# Revit family: Green Dot Sign® ADA Pictogram
name_source: partatom
category: Generic Models
units: mm (PartAtom-declared; Revit-internal decimal feet)

## family parameters
Always vertical = Yes
Can host rebar = No
Cut with Voids When Loaded = No
Host = Wall
Part Type = Normal
Room Calculation Point = No
Round Connector Dimension = Use Diameter
Shared = No

## types (48) — shared parameters
Height = 0' - 9 1/4"
Text Height = 0' - 0 5/8"
Text Line 3 = SAMPLE TEXT
Text Spacing = 0' - 0 3/8"
URL = https://www.greendotsign.com

## per-type parameters (varying)
| type | All Gender | All Gender Left | All Gender Right | Base Finish | Braille Finish | Chamfered Edge | Eased Edge | Men Restroom | Men Restroom Left | Men Restroom Right | Pictogram Finish | Text Block Height | Text Finish | Text Line 1 | Text Line 2 | Text Number of Lines | Thickness | Unisex Restroom | Unisex Restroom Left | Unisex Restroom Right | Width | Women Restroom | Women Restroom Left | Women Restroom Right |
| Aluminum Unisex Restroom Right 9.25 x 7.25 | No | No | No | Green Dot Sign® Red | Green Dot Sign® Red | No | Yes | No | No | No | Green Dot Sign® Aluminum | 0' - 2" | Green Dot Sign® Aluminum | RESTROOM | SAMPLE TEXT | 1 | 0' - 0 3/16" | No | No | Yes | 0' - 7 1/4" | No | No | No |
| Aluminum Unisex Restroom Left 9.25 x 7.25 | No | No | No | Green Dot Sign® Black | Green Dot Sign® Black | No | Yes | No | No | No | Green Dot Sign® Aluminum | 0' - 2" | Green Dot Sign® Aluminum | RESTROOM | SAMPLE TEXT | 1 | 0' - 0 3/16" | No | Yes | No | 0' - 7 1/4" | No | No | No |
| Aluminum All Gender Restroom Right 9.25 x 7.25 | No | No | No | Green Dot Sign® Red | Green Dot Sign® Red | No | Yes | No | No | Yes | Green Dot Sign® Aluminum | 0' - 2 3/4" | Green Dot Sign® Aluminum | ALL GENDER | RESTROOM | 2 | 0' - 0 3/16" | No | No | No | 0' - 7 1/4" | No | No | No |
| Aluminum All Gender Restroom Left 9.25 x 7.25 | No | Yes | No | Green Dot Sign® Black | Green Dot Sign® Black | No | Yes | No | No | No | Green Dot Sign® Aluminum | 0' - 2 3/4" | Green Dot Sign® Aluminum | ALL GENDER | RESTROOM | 2 | 0' - 0 3/16" | No | No | No | 0' - 7 1/4" | No | No | No |
| Aluminum Unisex Restroom 9.25 x 9.25 | No | No | No | Green Dot Sign® Black | Green Dot Sign® Black | No | Yes | No | No | No | Green Dot Sign® Aluminum | 0' - 2" | Green Dot Sign® Aluminum | RESTROOM | SAMPLE TEXT | 1 | 0' - 0 3/16" | Yes | No | No | 0' - 9 1/4" | No | No | No |
| Aluminum All Gender Restroom 9.25 x 7.25 | Yes | No | No | Green Dot Sign® Black | Green Dot Sign® Black | No | Yes | No | No | No | Green Dot Sign® Aluminum | 0' - 2 3/4" | Green Dot Sign® Aluminum | ALL GENDER | RESTROOM | 2 | 0' - 0 3/16" | No | No | No | 0' - 7 1/4" | No | No | No |
| Aluminum Women Restroom Right 9.25 x 7.25 | No | No | No | Green Dot Sign® Red | Green Dot Sign® Red | No | Yes | No | No | No | Green Dot Sign® Bronze | 0' - 2" | Green Dot Sign® Bronze | WOMEN | SAMPLE TEXT | 1 | 0' - 0 3/16" | No | No | No | 0' - 7 1/4" | No | No | Yes |
| Aluminum Women Restroom Left 9.25 x 7.25 | No | No | No | Green Dot Sign® Black | Green Dot Sign® Black | No | Yes | No | No | No | Green Dot Sign® Bronze | 0' - 2" | Green Dot Sign® Bronze | WOMEN | SAMPLE TEXT | 1 | 0' - 0 3/16" | No | No | No | 0' - 7 1/4" | No | Yes | No |
| Aluminum Men Restroom Right 9.25 x 7.25 | No | No | No | Green Dot Sign® Red | Green Dot Sign® Red | No | Yes | No | No | Yes | Green Dot Sign® Aluminum | 0' - 2" | Green Dot Sign® Aluminum | MEN | SAMPLE TEXT | 1 | 0' - 0 3/16" | No | No | No | 0' - 7 1/4" | No | No | No |
| Aluminum Men Restroom Left 9.25 x 7.25 | No | No | No | Green Dot Sign® Black | Green Dot Sign® Black | No | Yes | No | Yes | No | Green Dot Sign® Aluminum | 0' - 2" | Green Dot Sign® Aluminum | MEN | SAMPLE TEXT | 1 | 0' - 0 3/16" | No | No | No | 0' - 7 1/4" | No | No | No |
| Birch Plywood All Gender Restroom Right 9.25 x 7.25 | No | No | Yes | Green Dot Sign® Birch Plywood | Green Dot Sign® Dark Grey | No | Yes | No | No | No | Green Dot Sign® Dark Grey | 0' - 2 3/4" | Green Dot Sign® Dark Grey | ALL GENDER | RESTROOM | 2 | 0' - 0 11/16" | No | No | No | 0' - 7 1/4" | No | No | No |
| Birch Plywood All Gender Restroom Left 9.25 x 7.25 | No | Yes | No | Green Dot Sign® Birch Plywood | Green Dot Sign® Hot Pink | No | Yes | No | No | No | Green Dot Sign® Hot Pink | 0' - 2 3/4" | Green Dot Sign® Hot Pink | ALL GENDER | RESTROOM | 2 | 0' - 0 1/4" | No | No | No | 0' - 7 1/4" | No | No | No |
| Birch Plywood All Gender Restroom 9.25 x 7.25 | Yes | No | No | Green Dot Sign® Birch Plywood | Green Dot Sign® Light Blue | No | Yes | No | No | No | Green Dot Sign® Light Blue | 0' - 3" | Green Dot Sign® Light Blue | ALL GENDER | RESTROOM | 2 | 0' - 0 1/4" | No | No | No | 0' - 7 1/4" | No | No | No |
| Aspen Chamfered All Gender Restroom Right 9.25 x 7.25 | No | No | Yes | Green Dot Sign® Aspen | Green Dot Sign® Grey | Yes | No | No | No | No | Green Dot Sign® Grey | 0' - 2 3/4" | Green Dot Sign® Grey | ALL GENDER | RESTROOM | 2 | 0' - 0 11/16" | No | No | No | 0' - 7 1/4" | No | No | No |
| Aspen Chamfered All Gender Restroom Left 9.25 x 7.25 | No | Yes | No | Green Dot Sign® Aspen | Green Dot Sign® Purple | Yes | No | No | No | No | Green Dot Sign® Purple | 0' - 2 3/4" | Green Dot Sign® Purple | ALL GENDER | RESTROOM | 2 | 0' - 0 11/16" | No | No | No | 0' - 7 1/4" | No | No | No |
| Aspen Eased All Gender Restroom Right 9.25 x 7.25 | No | No | Yes | Green Dot Sign® Aspen | Green Dot Sign® Brown | No | Yes | No | No | No | Green Dot Sign® Brown | 0' - 2 3/4" | Green Dot Sign® Brown | ALL GENDER | RESTROOM | 2 | 0' - 0 11/16" | No | No | No | 0' - 7 1/4" | No | No | No |
| Aspen Eased All Gender Restroom Left 9.25 x 7.25 | No | Yes | No | Green Dot Sign® Aspen | Green Dot Sign® Blue | No | Yes | No | No | No | Green Dot Sign® Blue | 0' - 2 3/4" | Green Dot Sign® Blue | ALL GENDER | RESTROOM | 2 | 0' - 0 11/16" | No | No | No | 0' - 7 1/4" | No | No | No |
| Aspen Eased All Gender Restroom 9.25 x 7.25 | Yes | No | No | Green Dot Sign® Aspen | Green Dot Sign® Black | No | Yes | No | No | No | Green Dot Sign® Black | 0' - 2 3/4" | Green Dot Sign® Black | ALL GENDER | RESTROOM | 2 | 0' - 0 11/16" | No | No | No | 0' - 7 1/4" | No | No | No |
| Birch Plywood Unisex Restroom Right 9.25 x 7.25 | No | No | No | Green Dot Sign® Birch Plywood | Green Dot Sign® Purple | No | Yes | No | No | No | Green Dot Sign® Purple | 0' - 2" | Green Dot Sign® Purple | RESTROOM | SAMPLE TEXT | 1 | 0' - 0 11/16" | No | No | Yes | 0' - 7 1/4" | No | No | No |
| Birch Plywood Unisex Restroom Left 9.25 x 7.25 | No | No | No | Green Dot Sign® Birch Plywood | Green Dot Sign® Teal | No | Yes | No | No | No | Green Dot Sign® Teal | 0' - 2" | Green Dot Sign® Teal | RESTROOM | SAMPLE TEXT | 1 | 0' - 0 11/16" | No | Yes | No | 0' - 7 1/4" | No | No | No |
| Birch Plywood Unisex Restroom 9.25 x 9.25 | No | No | No | Green Dot Sign® Birch Plywood | Green Dot Sign® Orange | No | Yes | No | No | No | Green Dot Sign® Orange | 0' - 2" | Green Dot Sign® Orange | RESTROOM | SAMPLE TEXT | 1 | 0' - 0 11/16" | Yes | No | No | 0' - 9 1/4" | No | No | No |
| Aspen Chamfered Unisex Restroom Right 9.25 x 7.25 | No | No | No | Green Dot Sign® Aspen | Green Dot Sign® Blue | Yes | No | No | No | No | Green Dot Sign® Blue | 0' - 2" | Green Dot Sign® Blue | RESTROOM | SAMPLE TEXT | 1 | 0' - 0 11/16" | No | No | Yes | 0' - 7 1/4" | No | No | No |
| Aspen Chamfered Unisex Restroom Left 9.25 x 7.25 | No | No | No | Green Dot Sign® Aspen | Green Dot Sign® Forest Green | Yes | No | No | No | No | Green Dot Sign® Forest Green | 0' - 2" | Green Dot Sign® Forest Green | RESTROOM | SAMPLE TEXT | 1 | 0' - 0 11/16" | No | Yes | No | 0' - 7 1/4" | No | No | No |
| Aspen Chamfered Unisex Restroom 9.25 x 9.25 | No | No | No | Green Dot Sign® Aspen | Green Dot Sign® Red | Yes | No | No | No | No | Green Dot Sign® Red | 0' - 2" | Green Dot Sign® Red | RESTROOM | SAMPLE TEXT | 1 | 0' - 0 11/16" | Yes | No | No | 0' - 9 1/4" | No | No | No |
| Birch Plywood Women Restroom Right 9.25 x 7.25 | No | No | No | Green Dot Sign® Birch Plywood | Green Dot Sign® Forest Green | No | Yes | No | No | No | Green Dot Sign® Forest Green | 0' - 2" | Green Dot Sign® Forest Green | WOMEN | SAMPLE TEXT | 1 | 0' - 0 1/4" | No | No | No | 0' - 7 1/4" | No | No | Yes |
| Birch Plywood Women Restroom Left 9.25 x 7.25 | No | No | No | Green Dot Sign® Birch Plywood | Green Dot Sign® Red | No | Yes | No | No | No | Green Dot Sign® Red | 0' - 2" | Green Dot Sign® Red | WOMEN | SAMPLE TEXT | 1 | 0' - 0 1/4" | No | No | No | 0' - 7 1/4" | No | Yes | No |
| Birch Plywood Men Restroom Right 9.25 x 7.25 | No | No | No | Green Dot Sign® Birch Plywood | Green Dot Sign® Purple | No | Yes | No | No | Yes | Green Dot Sign® Purple | 0' - 2" | Green Dot Sign® Purple | MEN | SAMPLE TEXT | 1 | 0' - 0 1/4" | No | No | No | 0' - 7 1/4" | No | No | No |
| Birch Plywood Men Restroom Left 9.25 x 7.25 | No | No | No | Green Dot Sign® Birch Plywood | Green Dot Sign® Teal | No | Yes | No | Yes | No | Green Dot Sign® Teal | 0' - 2" | Green Dot Sign® Teal | MEN | SAMPLE TEXT | 1 | 0' - 0 1/4" | No | No | No | 0' - 7 1/4" | No | No | No |
| Aspen Chamfered Women Restroom Right 9.25 x 7.25 | No | No | No | Green Dot Sign® Aspen | Green Dot Sign® Kelly Green | Yes | No | No | No | No | Green Dot Sign® Kelly Green | 0' - 2" | Green Dot Sign® Kelly Green | WOMEN | SAMPLE TEXT | 1 | 0' - 0 11/16" | No | No | No | 0' - 7 1/4" | No | No | Yes |
| Aspen Chamfered Women Restroom Left 9.25 x 7.25 | No | No | No | Green Dot Sign® Aspen | Green Dot Sign® Dark Grey | Yes | No | No | No | No | Green Dot Sign® Dark Grey | 0' - 2" | Green Dot Sign® Dark Grey | WOMEN | SAMPLE TEXT | 1 | 0' - 0 11/16" | No | No | No | 0' - 7 1/4" | No | Yes | No |
| Aspen Chamfered Men Restroom Right 9.25 x 7.25 | No | No | No | Green Dot Sign® Aspen | Green Dot Sign® Blue | Yes | No | No | No | Yes | Green Dot Sign® Blue | 0' - 2" | Green Dot Sign® Blue | MEN | SAMPLE TEXT | 1 | 0' - 0 11/16" | No | No | No | 0' - 7 1/4" | No | No | No |
| Aspen Chamfered Men Restroom Left 9.25 x 7.25 | No | No | No | Green Dot Sign® Aspen | Green Dot Sign® Forest Green | Yes | No | No | Yes | No | Green Dot Sign® Forest Green | 0' - 2" | Green Dot Sign® Forest Green | MEN | SAMPLE TEXT | 1 | 0' - 0 11/16" | No | No | No | 0' - 7 1/4" | No | No | No |
| Aspen Chamfered Men Restroom 9.25 x 7.25 | No | No | No | Green Dot Sign® Aspen | Green Dot Sign® Red | Yes | No | Yes | No | No | Green Dot Sign® Red | 0' - 2" | Green Dot Sign® Red | MEN | SAMPLE TEXT | 1 | 0' - 0 11/16" | No | No | No | 0' - 7 1/4" | No | No | No |
| Aspen Eased Women Restroom Right 9.25 x 7.25 | No | No | No | Green Dot Sign® Aspen | Green Dot Sign® Orange | No | Yes | No | No | No | Green Dot Sign® Orange | 0' - 2" | Green Dot Sign® Orange | WOMEN | SAMPLE TEXT | 1 | 0' - 0 11/16" | No | No | No | 0' - 7 1/4" | No | No | Yes |
| Aspen Eased Women Restroom Left 9.25 x 7.25 | No | No | No | Green Dot Sign® Aspen | Green Dot Sign® Grey | No | Yes | No | No | No | Green Dot Sign® Grey | 0' - 2" | Green Dot Sign® Grey | WOMEN | SAMPLE TEXT | 1 | 0' - 0 11/16" | No | No | No | 0' - 7 1/4" | No | Yes | No |
| Aspen Eased Unisex Restroom Left 9.25 x 7.25 | No | No | No | Green Dot Sign® Aspen | Green Dot Sign® Kelly Green | No | Yes | No | No | No | Green Dot Sign® Kelly Green | 0' - 2" | Green Dot Sign® Kelly Green | RESTROOM | SAMPLE TEXT | 1 | 0' - 0 11/16" | No | Yes | No | 0' - 7 1/4" | No | No | No |
| Aspen Eased Unisex Restroom 9.25 x 9.25 | No | No | No | Green Dot Sign® Aspen | Green Dot Sign® Black | No | Yes | No | No | No | Green Dot Sign® Black | 0' - 2" | Green Dot Sign® Black | RESTROOM | SAMPLE TEXT | 1 | 0' - 0 11/16" | Yes | No | No | 0' - 9 1/4" | No | No | No |
| Aspen Eased Men Restroom Right 9.25 x 7.25 | No | No | No | Green Dot Sign® Aspen | Green Dot Sign® Light Blue | No | Yes | No | No | Yes | Green Dot Sign® Light Blue | 0' - 2" | Green Dot Sign® Light Blue | MEN | SAMPLE TEXT | 1 | 0' - 0 11/16" | No | No | No | 0' - 7 1/4" | No | No | No |
| Aspen Eased Men Restroom Left 9.25 x 7.25 | No | No | No | Green Dot Sign® Aspen | Green Dot Sign® Kelly Green | No | Yes | No | Yes | No | Green Dot Sign® Kelly Green | 0' - 2" | Green Dot Sign® Kelly Green | MEN | SAMPLE TEXT | 1 | 0' - 0 11/16" | No | No | No | 0' - 7 1/4" | No | No | No |
| Aspen Chamfered All Gender Restroom 9.25 x 7.25 | Yes | No | No | Green Dot Sign® Aspen | Green Dot Sign® Teal | Yes | No | No | No | No | Green Dot Sign® Teal | 0' - 3" | Green Dot Sign® Teal | ALL GENDER | RESTROOM | 2 | 0' - 0 11/16" | No | No | No | 0' - 7 1/4" | No | No | No |
| Aspen Eased Unisex Restroom Right 9.25 x 7.25 | No | No | No | Green Dot Sign® Aspen | Green Dot Sign® Light Blue | No | Yes | No | No | No | Green Dot Sign® Light Blue | 0' - 2" | Green Dot Sign® Light Blue | RESTROOM | SAMPLE TEXT | 1 | 0' - 0 11/16" | No | No | Yes | 0' - 7 1/4" | No | No | No |
| Aspen Chamfered Women Restroom 9.25 x 7.25 | No | No | No | Green Dot Sign® Aspen | Green Dot Sign® Hot Pink | Yes | No | No | No | No | Green Dot Sign® Hot Pink | 0' - 2" | Green Dot Sign® Hot Pink | WOMEN | SAMPLE TEXT | 1 | 0' - 0 11/16" | No | No | No | 0' - 7 1/4" | Yes | No | No |
| Aluminum Women Restroom 9.25 x 7.25 | No | No | No | Green Dot Sign® Black | Green Dot Sign® Black | No | Yes | No | No | No | Green Dot Sign® Bronze | 0' - 1 1/2" | Green Dot Sign® Bronze | WOMEN | SAMPLE TEXT | 1 | 0' - 0 3/16" | No | No | No | 0' - 7 1/4" | Yes | No | No |
| Aluminum Men Restroom 9.25 x 7.25 | No | No | No | Green Dot Sign® Black | Green Dot Sign® Black | No | Yes | Yes | No | No | Green Dot Sign® Aluminum | 0' - 2" | Green Dot Sign® Aluminum | MEN | SAMPLE TEXT | 1 | 0' - 0 3/16" | No | No | No | 0' - 7 1/4" | No | No | No |
| Aspen Eased Women Restroom 9.25 x 7.25 | No | No | No | Green Dot Sign® Aspen | Green Dot Sign® Black | No | Yes | No | No | No | Green Dot Sign® Black | 0' - 2" | Green Dot Sign® Black | WOMEN | SAMPLE TEXT | 1 | 0' - 0 11/16" | No | No | No | 0' - 7 1/4" | Yes | No | No |
| Birch Plywood Men Restroom 9.25 x 7.25 | No | No | No | Green Dot Sign® Birch Plywood | Green Dot Sign® Orange | No | Yes | Yes | No | No | Green Dot Sign® Orange | 0' - 2" | Green Dot Sign® Orange | MEN | SAMPLE TEXT | 1 | 0' - 0 1/4" | No | No | No | 0' - 7 1/4" | No | No | No |
| Birch Plywood Women Restroom 9.25 x 7.25 | No | No | No | Green Dot Sign® Birch Plywood | Green Dot Sign® Brown | No | Yes | No | No | No | Green Dot Sign® Brown | 0' - 2" | Green Dot Sign® Brown | WOMEN | SAMPLE TEXT | 1 | 0' - 0 1/4" | No | No | No | 0' - 7 1/4" | Yes | No | No |
| Aspen Eased Men Restroom 9.25 x 7.25 | No | No | No | Green Dot Sign® Aspen | Green Dot Sign® Black | No | Yes | Yes | No | No | Green Dot Sign® Black | 0' - 2" | Green Dot Sign® Black | MEN | SAMPLE TEXT | 1 | 0' - 0 11/16" | No | No | No | 0' - 7 1/4" | No | No | No |

## geometry (parser evidence)
native form markers: Sweep x11
no freeform markers — native parametric forms only
